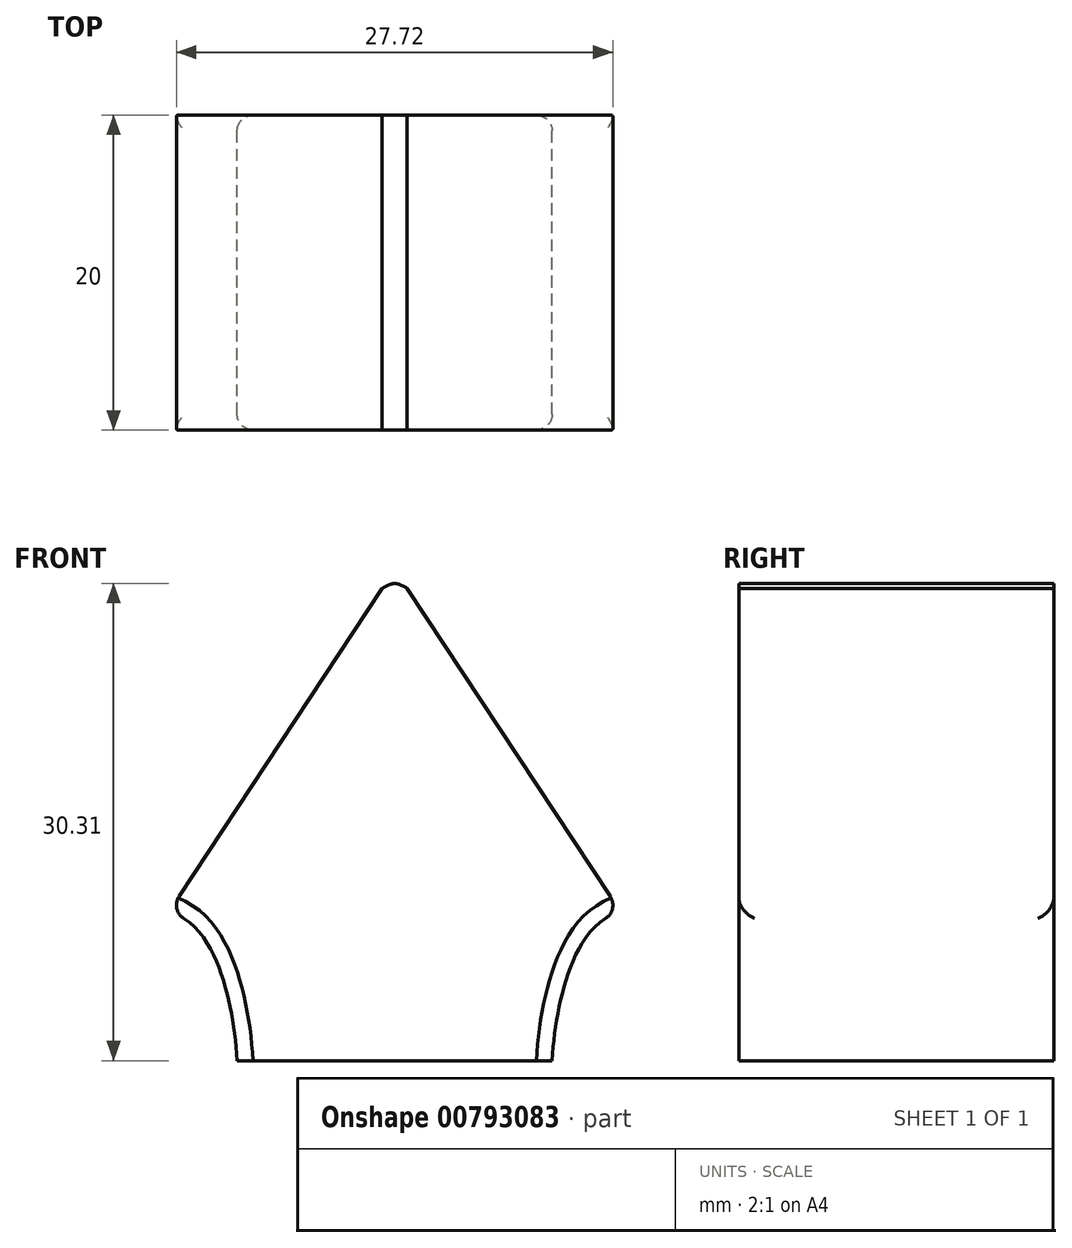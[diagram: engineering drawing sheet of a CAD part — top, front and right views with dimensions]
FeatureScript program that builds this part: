
annotation { "Feature Type Name" : "Feature", "Feature Type Description" : "" }
export const myFeature = defineFeature(function(context is Context, id is Id, definition is map)
    precondition{}
    {
        {
            var Q0;
            Q0=qCreatedBy(makeId("Front.planeOp"),FACE);
            var sketch = newSketch(context, id + "F0", { "sketchPlane" : qUnion([Q0])});
            skLineSegment(sketch, "E0", {"start": v(-17.88, 12) * mm, "end": v(-10, 0) * mm, "construction": true});
            skLineSegment(sketch, "E1", {"start": v(-13.94, 6) * mm, "end": v(-11.85, 7.37) * mm, "construction": true});
            skLineSegment(sketch, "E2", {"start": v(0, 0) * mm, "end": v(0, 30) * mm, "construction": true});
            skLineSegment(sketch, "E3", {"start": v(-10, 0) * mm, "end": v(0, 0) * mm});
            skLineSegment(sketch, "E4", {"start": v(-0.88, 50.38) * mm, "end": v(0, 50.38) * mm, "construction": true});
            skPoint(sketch, "E5", {"position": v(0, 51.09) * mm});
            skLineSegment(sketch, "E6", {"start": v(0, 50.38) * mm, "end": v(-0.5, 50.83) * mm, "construction": true});
            skFitSpline(sketch, "E7", {"points": [v(-0.88, 50.38) * mm, v(-0.5, 50.83) * mm, v(0, 51.09) * mm], "startDerivative": vector(0.55, 1.02) * mm, "endDerivative": vector(1.09, 0.4) * mm});
            skLineSegment(sketch, "E8.MirrorCS", {"start": v(10, 0) * mm, "end": v(0, 0) * mm});
            skFitSpline(sketch, "E9.MirrorCS", {"points": [v(0.88, 50.38) * mm, v(0.5, 50.83) * mm, v(0, 51.09) * mm], "startDerivative": vector(-0.55, 1.02) * mm, "endDerivative": vector(-1.09, 0.4) * mm});
            skLineSegment(sketch, "E10", {"start": v(-0.88, 50.38) * mm, "end": v(0.88, 50.38) * mm});
            skPoint(sketch, "E11", {"position": v(0, 30.31) * mm});
            skLineSegment(sketch, "E12", {"start": v(-0.8, 30) * mm, "end": v(-14.32, 9.47) * mm});
            skFitSpline(sketch, "E13", {"points": [v(-14.32, 9.47) * mm, v(-11.85, 7.37) * mm, v(-10, 0) * mm], "startDerivative": vector(8.21, -2.96) * mm, "endDerivative": vector(0.92, -15.16) * mm});
            skFitSpline(sketch, "E14.MirrorCS", {"points": [v(14.32, 9.47) * mm, v(11.85, 7.37) * mm, v(10, 0) * mm], "startDerivative": vector(-8.21, -2.96) * mm, "endDerivative": vector(-0.92, -15.16) * mm});
            skLineSegment(sketch, "E15.MirrorCS", {"start": v(0.8, 30) * mm, "end": v(14.32, 9.47) * mm});
            skFitSpline(sketch, "E16", {"points": [v(-0.8, 30) * mm, v(0, 30.31) * mm, v(0.8, 30) * mm], "startDerivative": vector(1.58, 0.94) * mm, "endDerivative": vector(1.58, -0.94) * mm});
            skSolve(sketch);
        }
        {
            var Q0;
            Q0=makeQuery(id+"F0.imprint","IMPRINT",FACE,{"disambiguationData":[TD([[makeQuery(id+"F0.imprint","IMPRINT",EDGE,{"derivedFrom":sQuery(id+"F0.wireOp",EDGE,"E3")}),1.0]])]});
            extrude(context, id + "F1", {"entities" : qUnion([Q0]), "depth" : 20 * mm, "offsetDistance" : 25 * mm});
        }
        {
            var Q0;
            Q0=makeQuery(id+"F1.opExtrude","SWEPT_EDGE",EDGE,{"disambiguationData":[OSD([sQuery(id+"F0.wireOp",EDGE,"kqauoslL-QG2K-Ny5p-njFf-08JwJWDmjOXk"),sQuery(id+"F0.wireOp",EDGE,"8ff87154-5a1e-4ab2-8533-8746f4c72040")])]});
            var Q1;
            Q1=makeQuery(id+"F1.opExtrude","SWEPT_EDGE",EDGE,{"disambiguationData":[OSD([sQuery(id+"F0.wireOp",EDGE,"a61ab567-d0b5-4428-87fe-cb8aecb609cd0.MirrorCS"),sQuery(id+"F0.wireOp",EDGE,"cb6749de-07f0-483e-a072-a5cbc38774c10.MirrorCS")])]});
            var Q2;
            Q2=makeQuery(id+"F1.opExtrude","SWEPT_EDGE",EDGE,{"disambiguationData":[OSD([sQuery(id+"F0.wireOp",EDGE,"E12"),sQuery(id+"F0.wireOp",EDGE,"E13")])]});
            var Q3;
            Q3=makeQuery(id+"F1.opExtrude","SWEPT_EDGE",EDGE,{"disambiguationData":[OSD([sQuery(id+"F0.wireOp",EDGE,"E14.MirrorCS"),sQuery(id+"F0.wireOp",EDGE,"E15.MirrorCS")])]});
            var Q4;
            Q4=makeQuery(id+"F1.opExtrude","CAP_EDGE",EDGE,{"disambiguationData":[OSD([sQuery(id+"F0.wireOp",EDGE,"E13")])],"isStart":true});
            var Q5;
            Q5=makeQuery(id+"F1.opExtrude","CAP_EDGE",EDGE,{"disambiguationData":[OSD([sQuery(id+"F0.wireOp",EDGE,"E13")])],"isStart":false});
            var Q6;
            Q6=makeQuery(id+"F1.opExtrude","CAP_EDGE",EDGE,{"disambiguationData":[OSD([sQuery(id+"F0.wireOp",EDGE,"E14.MirrorCS")])],"isStart":true});
            var Q7;
            Q7=makeQuery(id+"F1.opExtrude","CAP_EDGE",EDGE,{"disambiguationData":[OSD([sQuery(id+"F0.wireOp",EDGE,"E14.MirrorCS")])],"isStart":false});
            fillet(context, id + "F2", {"entities" : qUnion([Q0, Q1, Q2, Q3, Q4, Q5, Q6, Q7]), "radius" : 1 * mm, "tangentPropagation" : true, "allowEdgeOverflow" : false});
        }
    });
